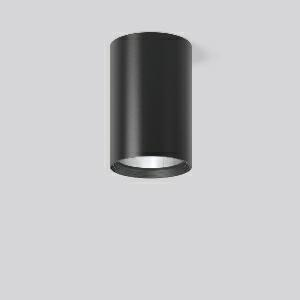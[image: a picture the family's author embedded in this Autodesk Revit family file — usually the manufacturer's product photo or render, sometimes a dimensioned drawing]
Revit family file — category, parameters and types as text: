
# Revit family: heledon_maxi_a_931226_003_3_76_bf76
name_source: partatom
category: Lighting Fixtures
units: mm (PartAtom-declared; Revit-internal decimal feet)

## family parameters
Cut with Voids When Loaded = No
Host = Face
Light Source = No
Part Type = Normal
Room Calculation Point = No
Round Connector Dimension = Use Diameter
Shared = No

## types (1)
- HELEDON maxi A (1 x LED Modul 935, 4200 lm, 3500)
    Apparent Load = 35 VA
    Approval mark = CE
    CIE Flux Codes = 97 100 100 100 100
    Color Rendering = 92
    Color Temperature = 3500
    Default Elevation = 1800 mm
    Description = Series: HELEDON maxi
Cylindrical surface-mounted downlight. Housing: die-cast aluminium, powder-coated. Internal ceiling frame polycarbonate with bayonet mounting. Black plastic ring and recessed LED to prevent glare from the side. Optical assembly with reflector made of MIRO-Silver with 98% total light reflection for outstanding efficiency - can be changed without tools. Best colour rendering index Ra>90. Suitable for Ceiling mounting. Easy installation with a separate ceiling frame with bayonet mounting and plug connection. Driver integrated. Connected via plug-in connector. High quality converter without flickering and stroboscopic effect. The following accessories can be mounted without use of tools: interchangeable lenses, decorative glasses, honeycomb louvre, clear and frosted diffusers, white interchangeable plastic ring. 
Colour: deep black, matt (RAL 9005)
Diameter: 123 mm
Height: 183 mm
Lamp: LED
Socket: without socket
Colour temperature: 3500K
Colour rendering index (CRI): 92
System power: 35 W
Rated luminous flux: 4200 lm
Luminous efficiency: 120 lm/W
Control gear: Converter, dimmable, DALI
Protection class: I
Type of protection: IP 20
    Height = 183 mm
    Lamp = 1 x LED Modul 935
    Lamp Light Flux = 4200 lm
    Lamp count = 1
    Length = 123 mm
    Lifetime = 50000 h
    Luminous efficacy = 120 lm/W
    Manufacturer = RZB
    ModVariant = No
    Model = 931226.003.3.76
    Mounting Place = Ceiling
    Mounting Type = Surface mounted
    Number of Poles = 1
    OnlyDefault = Yes
    Power Factor = 1
    Product Name = HELEDON maxi A
    Product group = Surface mounted downlights
    ProductGroupID = 302
    Protection Class = Protection class I
    Protection Degree = IP 20
    RLX_Detail_Level = 1
    RLX_Emergency_Light_Flux = 0 lm
    RLX_Emergency_Type = 0
    RLX_Emergency_Type_DB = No
    RlxData = <blob elided: 97745 chars, md5=3b8d633f>
    Socket = socket
    Standby Power = 0 W
    System Light Flux = 4200 lm
    System Power = 35 W
    Type Comments = Product without accessories
    Type Image = 931192.003.jpg
    URL = http://relux.com
    VarID = ---
    Voltage = 230 V
    Voltage Range = 220-240 V
    Weight = 0.00 kg
    Width = 0 mm  [stored 0 ft]

note: [stored X ft] marks values corroborated as IEEE doubles in the binary element streams (Revit-internal decimal feet)

## geometry (parser evidence)
native form markers: Blend x4, Sweep x10
no freeform markers — native parametric forms only
